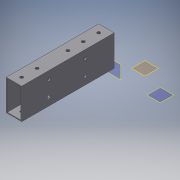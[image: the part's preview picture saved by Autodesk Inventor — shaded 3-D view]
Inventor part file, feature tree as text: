
AUTODESK INVENTOR PART (.ipt)
format: ipt  version: 2018 (Build 220112000, 112)  size: 166,400 bytes
history: native  units: in
note: dims shown in document units (in); Inventor stores cm internally (conversion verified against a paired STEP export)
features: plane x4, extrude x4, sketch x4
ambient origin geometry x8: Origin, YZ Plane, XZ Plane, XY Plane, X Axis, Y Axis, Z Axis, Center Point
bodies: Body1 (feature_tree)
feature tree (12):
  plane  "Work Plane1"
  extrude  "Extrusion16"  TaperAngle=0.0deg  [1 undecoded]
  plane  "Work Plane4"
  extrude  "Extrusion17"  Depth=6.0in
  plane  "Work Plane3"
  extrude  "Extrusion22"  Depth=0.5in
  plane  "Work Plane2"
  extrude  "Extrusion23"  Depth=2.0in
  sketch  "Sketch20"  dims[d71=1.0in d72=2.0in d73=0.065in d74=0.065in d75=0.065in d76=0.065in d77=0.1in d78=0.0in]
  sketch  "Sketch21"  dims[d79=6.0in d80=0.0in d81=0.5in]
  sketch  "Sketch26"  dims[d82=0.5in d83=0.5in]
  sketch  "Sketch27"  dims[d84=1.0in d85=0.5in d86=0.2031in d87=0.2031in d88=0.2031in d89=1.0in d90=1.0in d91=1.0in d92=0.2031in d93=0.2031in d94=0.5in d95=0.5in d96=3.0in d97=0.0in d122=0.2031in d123=1.765in d124=0.491in d125=0.2031in d126=2.355in d129=1.0in d130=0.2031in d131=1.0in d132=0.2031in d133=1.0in d134=0.0in d135=0.5in d136=0.5in d137=1.5in d138=0.5in d139=0.2031in d140=0.2031in d141=2.0in d142=0.0in]
note: 1 required parameter value undecoded (feature->parameter linkage not recoverable at this tier; creation-order binding heuristic only, values carry confidence <= 0.55)
